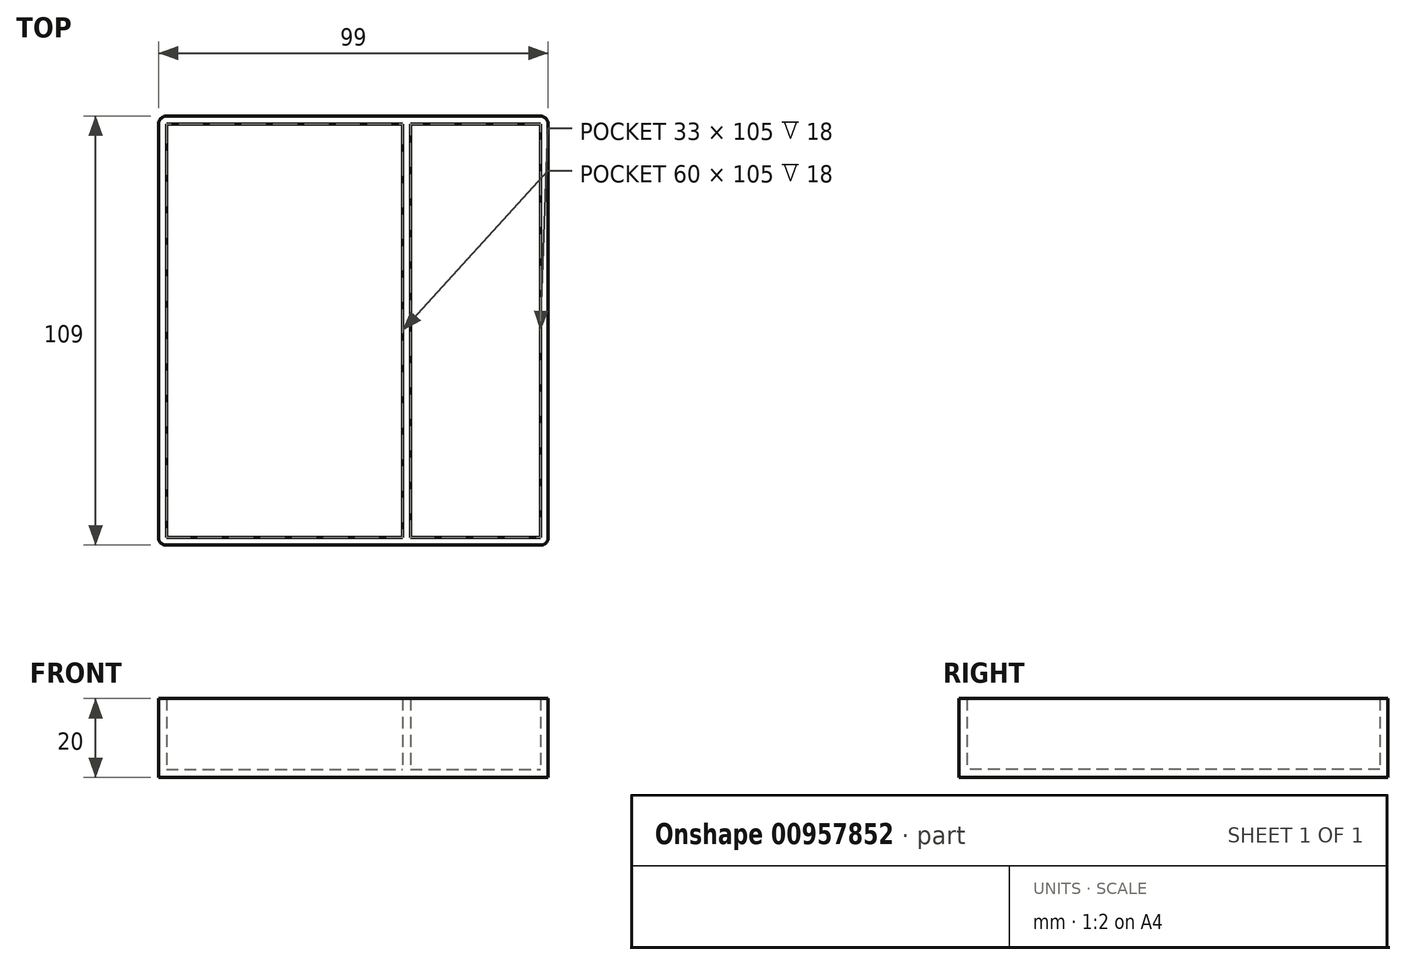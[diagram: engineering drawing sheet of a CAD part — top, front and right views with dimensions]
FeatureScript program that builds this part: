
annotation { "Feature Type Name" : "Feature", "Feature Type Description" : "" }
export const myFeature = defineFeature(function(context is Context, id is Id, definition is map)
    precondition{}
    {
        {
            var Q0;
            Q0=qCreatedBy(makeId("Top.planeOp"),FACE);
            var sketch = newSketch(context, id + "F0", { "sketchPlane" : qUnion([Q0])});
            skLineSegment(sketch, "E0.bottom", {"start": v(-48.26, 57.56) * mm, "end": v(50.74, 57.56) * mm});
            skLineSegment(sketch, "E0.top", {"start": v(-48.26, -51.44) * mm, "end": v(50.74, -51.44) * mm});
            skLineSegment(sketch, "E0.left", {"start": v(-48.26, 57.56) * mm, "end": v(-48.26, -51.44) * mm});
            skLineSegment(sketch, "E0.right", {"start": v(50.74, 57.56) * mm, "end": v(50.74, -51.44) * mm});
            skSolve(sketch);
        }
        {
            var Q0;
            Q0=makeQuery(id+"F0.imprint","IMPRINT",FACE,{"disambiguationData":[TD([[makeQuery(id+"F0.imprint","IMPRINT",EDGE,{"derivedFrom":sQuery(id+"F0.wireOp",EDGE,"E0.bottom")}),-1.0]])]});
            extrude(context, id + "F1", {"entities" : qUnion([Q0]), "depth" : 20 * mm, "offsetDistance" : 25 * mm});
        }
        {
            var Q0;
            Q0=makeQuery(id+"F1.opExtrude","CAP_FACE",FACE,{"disambiguationData":[OSD([sQuery(id+"F0.wireOp",EDGE,"E0.bottom"),sQuery(id+"F0.wireOp",EDGE,"E0.top"),sQuery(id+"F0.wireOp",EDGE,"E0.left"),sQuery(id+"F0.wireOp",EDGE,"E0.right")])],"isStart":false});
            shell(context, id + "F2", {"entities" : qUnion([Q0]), "thickness" : 2 * mm});
        }
        {
            var Q0;
            Q0=makeQuery(id+"F2.opShell","OFFSET_FACE",FACE,{"disambiguationData":[OSD([sQuery(id+"F0.wireOp",EDGE,"E0.bottom"),sQuery(id+"F0.wireOp",EDGE,"E0.top"),sQuery(id+"F0.wireOp",EDGE,"E0.left"),sQuery(id+"F0.wireOp",EDGE,"E0.right")])]});
            var sketch = newSketch(context, id + "F3", { "sketchPlane" : qUnion([Q0])});
            skLineSegment(sketch, "E1.bottom", {"start": v(13.74, 55.56) * mm, "end": v(15.74, 55.56) * mm});
            skLineSegment(sketch, "E1.top", {"start": v(13.74, -49.44) * mm, "end": v(15.74, -49.44) * mm});
            skLineSegment(sketch, "E1.left", {"start": v(13.74, 55.56) * mm, "end": v(13.74, -49.44) * mm});
            skLineSegment(sketch, "E1.right", {"start": v(15.74, 55.56) * mm, "end": v(15.74, -49.44) * mm});
            skSolve(sketch);
        }
        {
            var Q0;
            Q0=makeQuery(id+"F3.imprint","IMPRINT",FACE,{"disambiguationData":[TD([[makeQuery(id+"F3.imprint","IMPRINT",EDGE,{"derivedFrom":sQuery(id+"F3.wireOp",EDGE,"E1.bottom")}),-1.0]])]});
            var Q1;
            Q1=makeQuery(id+"F1.opExtrude","CAP_FACE",FACE,{"disambiguationData":[OSD([sQuery(id+"F0.wireOp",EDGE,"E0.bottom"),sQuery(id+"F0.wireOp",EDGE,"E0.top"),sQuery(id+"F0.wireOp",EDGE,"E0.left"),sQuery(id+"F0.wireOp",EDGE,"E0.right")])],"isStart":false});
            extrude(context, id + "F4", {"entities" : qUnion([Q0]), "operationType" : NewBodyOperationType.ADD, "endBound" : BoundingType.UP_TO_SURFACE, "depth" : 25 * mm, "endBoundEntityFace" : qUnion([Q1]), "offsetDistance" : 25 * mm});
        }
        {
            var Q0;
            Q0=makeQuery(id+"F1.opExtrude","SWEPT_EDGE",EDGE,{"disambiguationData":[OSD([sQuery(id+"F0.wireOp",EDGE,"E0.bottom"),sQuery(id+"F0.wireOp",EDGE,"E0.left")])]});
            var Q1;
            Q1=makeQuery(id+"F1.opExtrude","SWEPT_EDGE",EDGE,{"disambiguationData":[OSD([sQuery(id+"F0.wireOp",EDGE,"E0.top"),sQuery(id+"F0.wireOp",EDGE,"E0.left")])]});
            var Q2;
            Q2=makeQuery(id+"F1.opExtrude","SWEPT_EDGE",EDGE,{"disambiguationData":[OSD([sQuery(id+"F0.wireOp",EDGE,"E0.top"),sQuery(id+"F0.wireOp",EDGE,"E0.right")])]});
            var Q3;
            Q3=makeQuery(id+"F1.opExtrude","SWEPT_EDGE",EDGE,{"disambiguationData":[OSD([sQuery(id+"F0.wireOp",EDGE,"E0.bottom"),sQuery(id+"F0.wireOp",EDGE,"E0.right")])]});
            fillet(context, id + "F5", {"entities" : qUnion([Q0, Q1, Q2, Q3]), "radius" : 2 * mm, "tangentPropagation" : true, "allowEdgeOverflow" : false});
        }
    });
